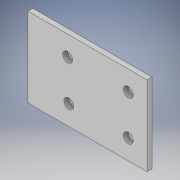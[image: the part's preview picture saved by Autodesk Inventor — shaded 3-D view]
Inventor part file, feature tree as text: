
AUTODESK INVENTOR PART (.ipt)
format: ipt  version: 2017 (Build 210142000, 142)  size: 104,448 bytes
history: native  units: in
note: dims shown in document units (in); Inventor stores cm internally (conversion verified against a paired STEP export)
features: extrude x1, sketch x1
ambient origin geometry x8: Origin, YZ Plane, XZ Plane, XY Plane, X Axis, Y Axis, Z Axis, Center Point
bodies: Solid1 (feature_tree)
feature tree (2):
  extrude  "Extrusion1"  Depth=2.0in
  sketch  "Sketch1"  dims[d0=3.0in d1=2.0in d2=0.25in d3=0.25in d4=1.0in d5=0.5in d6=1.0in d7=0.25in d8=0.25in d9=1.0in d10=0.125in d11=0.0in d12=0.5in]
